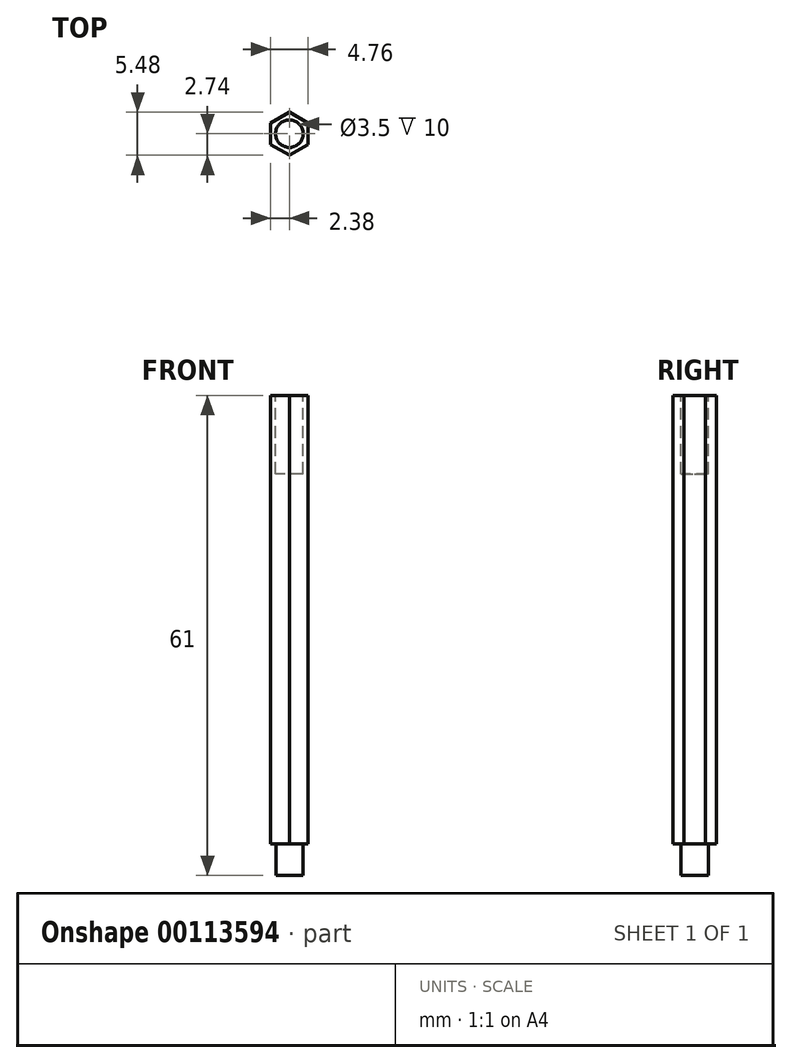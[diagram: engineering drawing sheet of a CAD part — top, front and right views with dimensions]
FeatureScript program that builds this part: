
annotation { "Feature Type Name" : "Feature", "Feature Type Description" : "" }
export const myFeature = defineFeature(function(context is Context, id is Id, definition is map)
    precondition{}
    {
        {
            var Q0;
            Q0=qCreatedBy(makeId("Top.planeOp"),FACE);
            var sketch = newSketch(context, id + "F0", { "sketchPlane" : qUnion([Q0])});
            skCircle(sketch, "E0.cCircle", {"center": v(0, 0) * mm, "radius": 2.38 * mm, "construction": true});
            skLineSegment(sketch, "E0.0", {"start": v(0, 2.74) * mm, "end": v(2.37, 1.37) * mm});
            skLineSegment(sketch, "E0.1", {"start": v(2.37, 1.37) * mm, "end": v(2.38, -1.37) * mm});
            skLineSegment(sketch, "E0.2", {"start": v(2.38, -1.37) * mm, "end": v(0, -2.74) * mm});
            skLineSegment(sketch, "E0.3", {"start": v(0, -2.74) * mm, "end": v(-2.37, -1.37) * mm});
            skLineSegment(sketch, "E0.4", {"start": v(-2.37, -1.37) * mm, "end": v(-2.38, 1.37) * mm});
            skLineSegment(sketch, "E0.5", {"start": v(-2.37, 1.37) * mm, "end": v(0, 2.74) * mm});
            skPoint(sketch, "E0.0.midPoint", {"position": v(1.19, 2.06) * mm});
            skSolve(sketch);
        }
        {
            var Q0;
            Q0 = qSketchRegion(id + "F0", true);
            extrude(context, id + "F1", {"entities" : qUnion([Q0]), "depth" : 57 * mm});
        }
        {
            var Q0;
            Q0=makeQuery(id+"F1.opExtrude","CAP_FACE",FACE,{"disambiguationData":[OSD([sQuery(id+"F0.wireOp",EDGE,"E0.0"),sQuery(id+"F0.wireOp",EDGE,"E0.1"),sQuery(id+"F0.wireOp",EDGE,"E0.2"),sQuery(id+"F0.wireOp",EDGE,"E0.3"),sQuery(id+"F0.wireOp",EDGE,"E0.4"),sQuery(id+"F0.wireOp",EDGE,"E0.5")])],"isStart":false});
            var sketch = newSketch(context, id + "F2", { "sketchPlane" : qUnion([Q0])});
            skCircle(sketch, "E1", {"center": v(0, 0) * mm, "radius": 1.75 * mm});
            skSolve(sketch);
        }
        {
            var Q0;
            Q0=makeQuery(id+"F2.imprint","IMPRINT",FACE,{"disambiguationData":[TD([[makeQuery(id+"F2.imprint","IMPRINT",EDGE,{"derivedFrom":sQuery(id+"F2.wireOp",EDGE,"E1")}),1.0]])]});
            extrude(context, id + "F3", {"entities" : qUnion([Q0]), "operationType" : NewBodyOperationType.REMOVE, "oppositeDirection" : true, "depth" : 10 * mm});
        }
        {
            var Q0;
            Q0=makeQuery(id+"F1.opExtrude","CAP_FACE",FACE,{"disambiguationData":[OSD([sQuery(id+"F0.wireOp",EDGE,"E0.0"),sQuery(id+"F0.wireOp",EDGE,"E0.1"),sQuery(id+"F0.wireOp",EDGE,"E0.2"),sQuery(id+"F0.wireOp",EDGE,"E0.3"),sQuery(id+"F0.wireOp",EDGE,"E0.4"),sQuery(id+"F0.wireOp",EDGE,"E0.5")])],"isStart":true});
            var sketch = newSketch(context, id + "F4", { "sketchPlane" : qUnion([Q0])});
            skCircle(sketch, "E2", {"center": v(0, 0) * mm, "radius": 1.73 * mm});
            skSolve(sketch);
        }
        {
            var Q0;
            Q0 = qSketchRegion(id + "F4", true);
            extrude(context, id + "F5", {"entities" : qUnion([Q0]), "operationType" : NewBodyOperationType.ADD, "depth" : 4 * mm});
        }
    });
